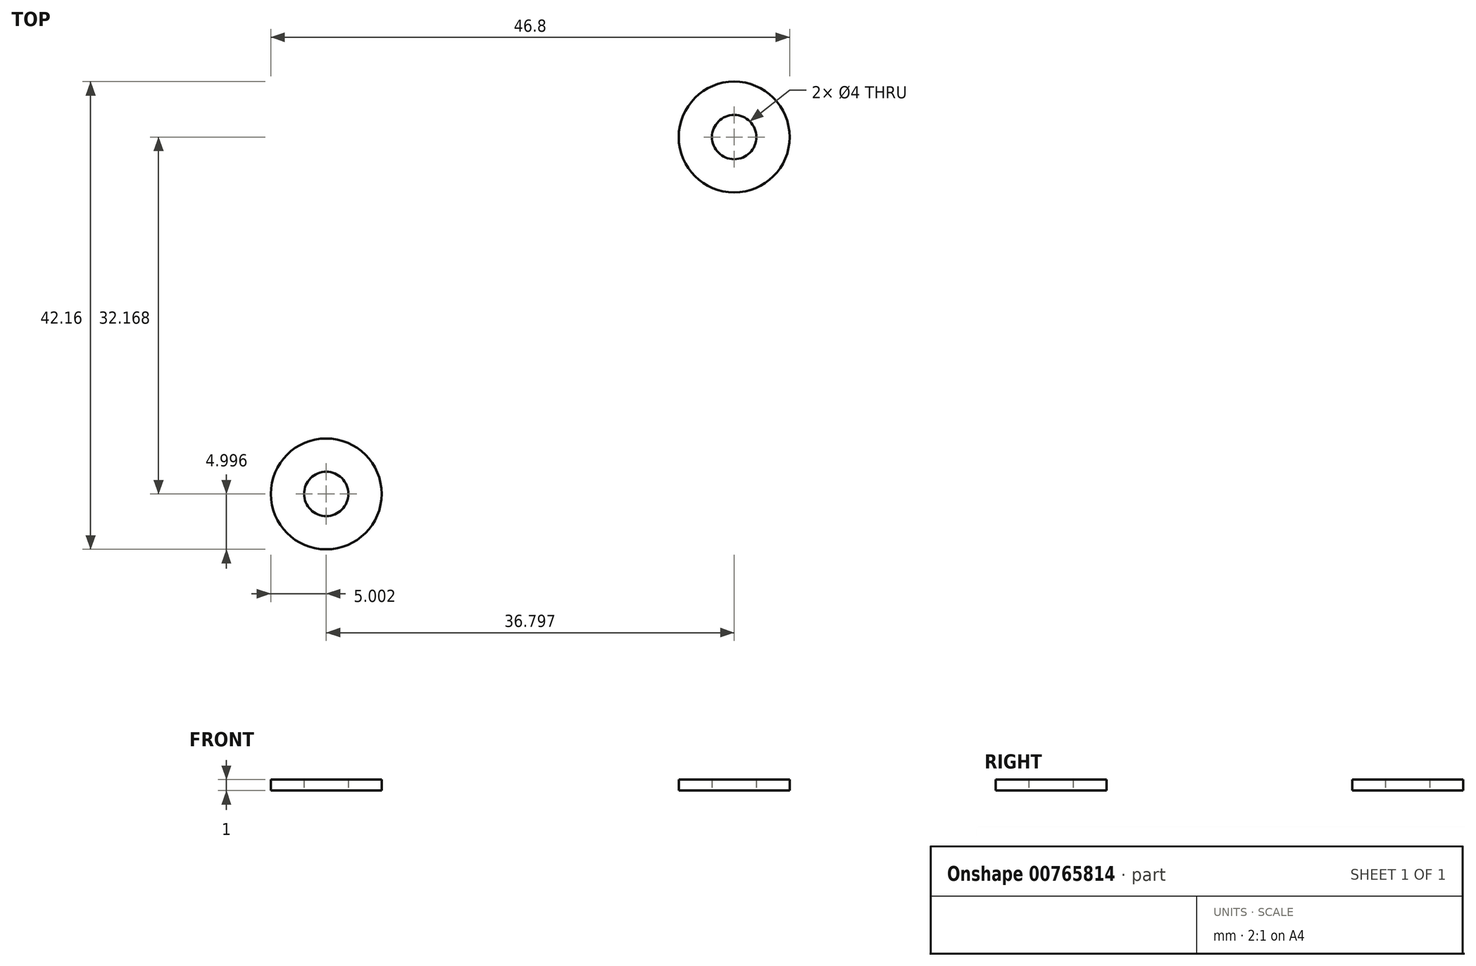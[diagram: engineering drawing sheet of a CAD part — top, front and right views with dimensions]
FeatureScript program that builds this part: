
annotation { "Feature Type Name" : "Feature", "Feature Type Description" : "" }
export const myFeature = defineFeature(function(context is Context, id is Id, definition is map)
    precondition{}
    {
        {
            var Q0;
            Q0=qCreatedBy(makeId("Top.planeOp"),FACE);
            var sketch = newSketch(context, id + "F0", { "sketchPlane" : qUnion([Q0])});
            skCircle(sketch, "E0", {"center": v(18.4, 16.08) * mm, "radius": 2 * mm});
            skCircle(sketch, "E1", {"center": v(18.4, 16.08) * mm, "radius": 5 * mm});
            skCircle(sketch, "E2.MirrorC", {"center": v(18.4, -16.08) * mm, "radius": 5 * mm});
            skCircle(sketch, "E3.MirrorC", {"center": v(18.4, -16.08) * mm, "radius": 2 * mm});
            skCircle(sketch, "E4.MirrorC", {"center": v(-18.4, 16.08) * mm, "radius": 5 * mm});
            skCircle(sketch, "E5.MirrorC", {"center": v(-18.4, -16.08) * mm, "radius": 5 * mm});
            skCircle(sketch, "E6.MirrorC", {"center": v(-18.4, -16.08) * mm, "radius": 2 * mm});
            skCircle(sketch, "E7.MirrorC", {"center": v(-18.4, 16.08) * mm, "radius": 2 * mm});
            skSolve(sketch);
        }
        {
            var Q0;
            Q0=makeQuery(id+"F0.imprint","IMPRINT",FACE,{"disambiguationData":[TD([[makeQuery(id+"F0.imprint","IMPRINT",EDGE,{"derivedFrom":sQuery(id+"F0.wireOp",EDGE,"E4.MirrorC")}),-1.0]])]});
            var Q1;
            Q1=makeQuery(id+"F0.imprint","IMPRINT",FACE,{"disambiguationData":[TD([[makeQuery(id+"F0.imprint","IMPRINT",EDGE,{"derivedFrom":sQuery(id+"F0.wireOp",EDGE,"E5.MirrorC")}),1.0]])]});
            var Q2;
            Q2=makeQuery(id+"F0.imprint","IMPRINT",FACE,{"disambiguationData":[TD([[makeQuery(id+"F0.imprint","IMPRINT",EDGE,{"derivedFrom":sQuery(id+"F0.wireOp",EDGE,"E2.MirrorC")}),-1.0]])]});
            var Q3;
            Q3=makeQuery(id+"F0.imprint","IMPRINT",FACE,{"disambiguationData":[TD([[makeQuery(id+"F0.imprint","IMPRINT",EDGE,{"derivedFrom":sQuery(id+"F0.wireOp",EDGE,"E0")}),-1.0]])]});
            extrude(context, id + "F1", {"entities" : qUnion([Q0, Q1, Q2, Q3]), "depth" : 1 * mm, "offsetDistance" : 25 * mm});
        }
    });
